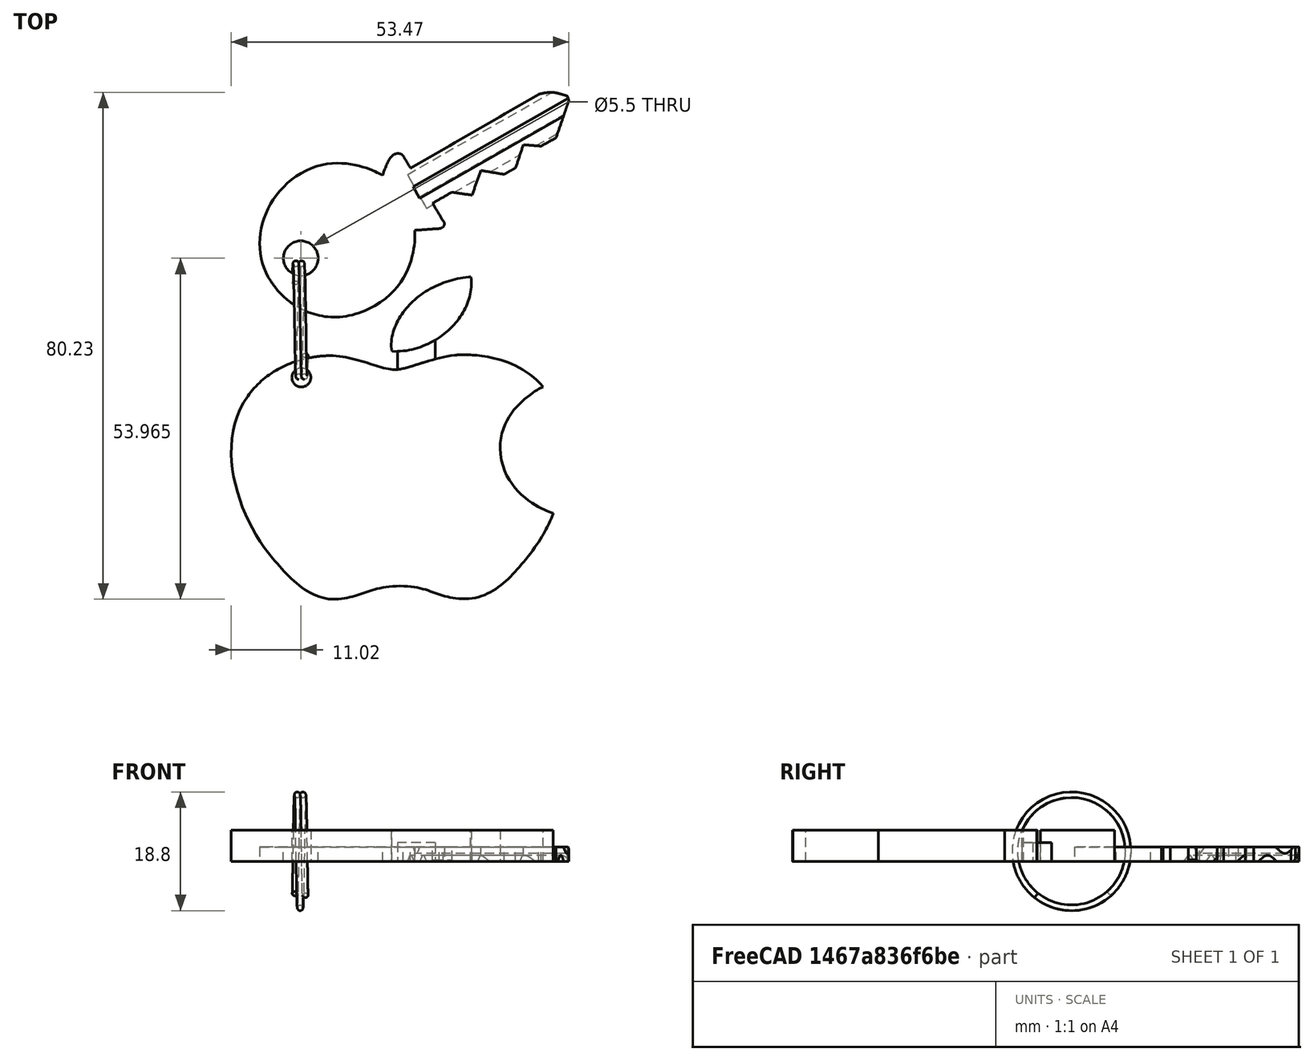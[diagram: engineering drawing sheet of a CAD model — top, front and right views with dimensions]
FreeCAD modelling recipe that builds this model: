
FCSTD DOCUMENT  (FreeCAD 0.14R3703 (Git))
Label: Mac_Keychain
License: CC-BY 3.0
LicenseURL: http://creativecommons.org/licenses/by/3.0/
objects: Part::Feature×4, Part::Extrusion×2, Part::Box×1, Part::MultiFuse×1, Sketcher::SketchObject×1, PartDesign::Pocket×1, App::DocumentObjectGroup×1
note: 11 computed .brp shape members not serialized (recipe doc carries the construction recipe); baked Part::Feature solids carry a one-line shape summary decoded from their .brp

FEATURE [Part::Feature] path2850
  shape: bbox 52.07 x 39.11 x 2e-07 mm, 0 faces, 0 solids (baked)
FEATURE [Part::Feature] path2850001
  shape: bbox 13.11 x 11.96 x 2e-07 mm, 0 faces, 0 solids (baked)
FEATURE [Part::Extrusion] Extrude  label="Manzana"
  Base = -> path2850
  Dir = (0,0,5)
  Solid = true
FEATURE [Part::Extrusion] Extrude001  label="Hoja"
  Base = -> path2850001
  Dir = (0,0,5)
  Solid = true
FEATURE [Part::Box] Box  label="Union"
  Height = 3
  Length = 6
  Placement = pos=(26,-19,0) rot=(0,0,1;0rad)
  Width = 11
FEATURE [Part::MultiFuse] Fusion  label="mac"
  Shapes = -> [Box,Extrude001,Extrude]
FEATURE [Sketcher::SketchObject] Sketch
  Placement = pos=(0,0,5) rot=(0,0,1;0rad)
  Support = -> Fusion [Face4]
  sketch-geometry (1):
    g0: Circle CenterX=10.7874 CenterY=-16.3307 CenterZ=0 NormalX=0 NormalY=0 NormalZ=1 Radius=1.5
  constraints (1):
    c: Radius(g0) = 1.5
FEATURE [PartDesign::Pocket] Pocket  label="Keychain_final"
  Length = 5
  Sketch = -> Sketch
  Type = 0
FEATURE [Part::Feature] Cut  label="key-model-1"
  Placement = pos=(5.53024,-0.4,0) rot=(0,0,1;0.517888rad)
  shape: bbox 49.82 x 36.6 x 2.3 mm, 44 faces (baked)
FEATURE [Part::Feature] Sweep  label="key-ring-model-1"
  Placement = pos=(9.8,-7.2454,1.6391) rot=(0.333333,0.881917,0.333333;1.69612rad)
  shape: bbox 3.31 x 27.02 x 26.33 mm, 4 faces (baked)
FEATURE [App::DocumentObjectGroup] Group  label="Assembly"
  Group = -> [Sweep,Cut]
